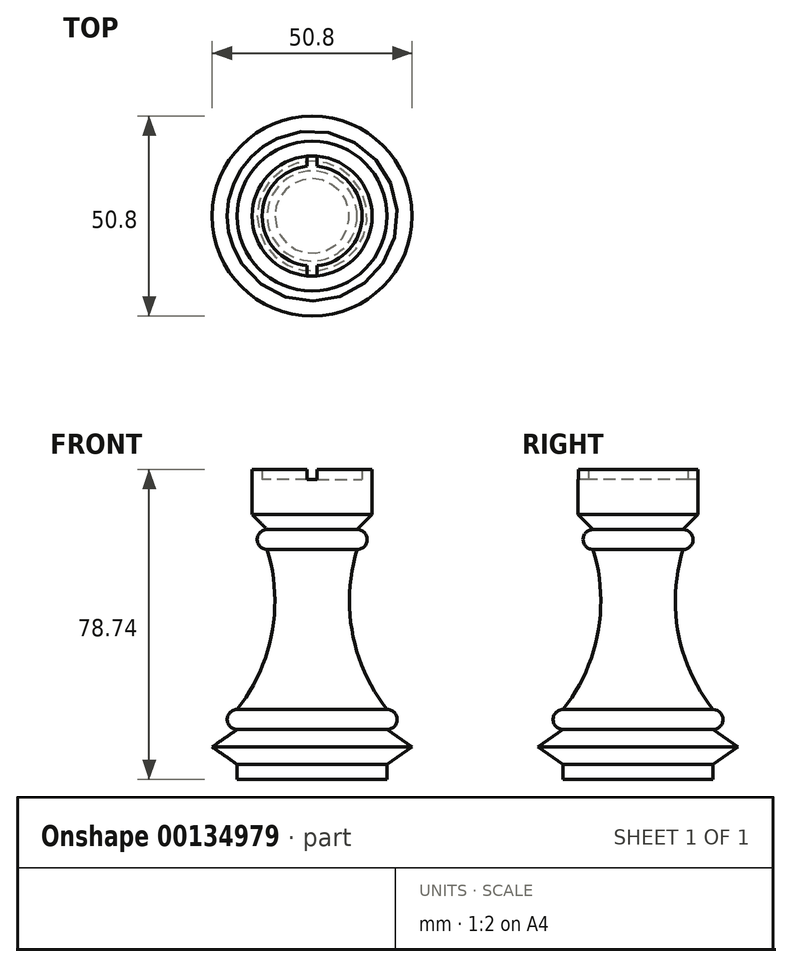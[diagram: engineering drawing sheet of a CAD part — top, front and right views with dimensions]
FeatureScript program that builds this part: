
annotation { "Feature Type Name" : "Feature", "Feature Type Description" : "" }
export const myFeature = defineFeature(function(context is Context, id is Id, definition is map)
    precondition{}
    {
        {
            var Q0;
            Q0=qCreatedBy(makeId("Front.planeOp"),FACE);
            var sketch = newSketch(context, id + "F0", { "sketchPlane" : qUnion([Q0])});
            skLineSegment(sketch, "E0", {"start": v(0, 0) * mm, "end": v(19.05, 0) * mm});
            skLineSegment(sketch, "E1", {"start": v(19.05, 0) * mm, "end": v(19.05, 3.8) * mm});
            skLineSegment(sketch, "E2", {"start": v(19.05, 3.81) * mm, "end": v(25.4, 8.26) * mm});
            skLineSegment(sketch, "E3", {"start": v(25.4, 8.25) * mm, "end": v(19.05, 12.7) * mm});
            skLineSegment(sketch, "E4", {"start": v(0, 0) * mm, "end": v(0, 76.2) * mm});
            skLineSegment(sketch, "E5", {"start": v(0, 76.2) * mm, "end": v(12.7, 76.2) * mm});
            skLineSegment(sketch, "E6", {"start": v(12.7, 76.2) * mm, "end": v(12.7, 78.74) * mm});
            skLineSegment(sketch, "E7", {"start": v(12.7, 78.74) * mm, "end": v(15.24, 78.74) * mm});
            skLineSegment(sketch, "E8", {"start": v(15.24, 78.74) * mm, "end": v(15.24, 67.31) * mm});
            skLineSegment(sketch, "E9", {"start": v(15.24, 67.31) * mm, "end": v(11.43, 63.5) * mm});
            skArc(sketch, "E10", {"start": v(11.43, 58.42) * mm, "mid": v(13.97, 60.96) * mm, "end": v(11.43, 63.5) * mm});
            skArc(sketch, "E11", {"start": v(19.05, 12.7) * mm, "mid": v(21.6, 15.24) * mm, "end": v(19.05, 17.78) * mm});
            skArc(sketch, "E12", {"start": v(11.43, 58.42) * mm, "mid": v(10.23, 37.16) * mm, "end": v(19.05, 17.78) * mm});
            skSolve(sketch);
        }
        {
            var Q0;
            Q0 = qSketchRegion(id + "F0", true);
            var Q1;
            Q1=sQuery(id+"F0.wireOp",EDGE,"E4");
            revolve(context, id + "F1", {"entities" : qUnion([Q0]), "axis" : qUnion([Q1]), "revolveType" : RevolveType.FULL});
        }
        {
            var Q0;
            Q0=qCreatedBy(makeId("Front.planeOp"),FACE);
            var sketch = newSketch(context, id + "F2", { "sketchPlane" : qUnion([Q0])});
            skLineSegment(sketch, "E13.bottom", {"start": v(1.27, 78.74) * mm, "end": v(-1.27, 78.74) * mm});
            skLineSegment(sketch, "E13.top", {"start": v(1.27, 76.2) * mm, "end": v(-1.27, 76.2) * mm});
            skLineSegment(sketch, "E13.left", {"start": v(1.27, 78.74) * mm, "end": v(1.27, 76.2) * mm});
            skLineSegment(sketch, "E13.right", {"start": v(-1.27, 78.74) * mm, "end": v(-1.27, 76.2) * mm});
            skPoint(sketch, "E13.middle", {"position": v(0, 77.47) * mm});
            skSolve(sketch);
        }
        {
            var Q0;
            Q0 = qSketchRegion(id + "F2", true);
            extrude(context, id + "F3", {"entities" : qUnion([Q0]), "operationType" : NewBodyOperationType.REMOVE, "oppositeDirection" : true, "depth" : 25.4 * mm, "hasSecondDirection" : true, "secondDirectionBound" : SecondDirectionBoundingType.THROUGH_ALL, "secondDirectionOppositeDirection" : false, "secondDirectionDepth" : 25.4 * mm});
        }
    });
